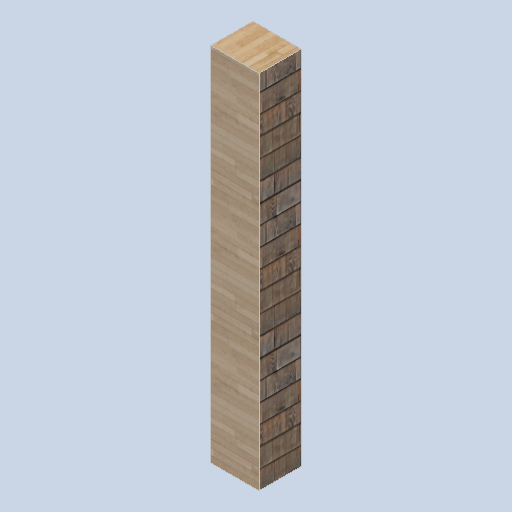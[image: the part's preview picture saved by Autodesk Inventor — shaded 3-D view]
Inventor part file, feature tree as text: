
AUTODESK INVENTOR PART (.ipt)
format: ipt  version: 2024.2 (Build 282272000, 272)  size: 173,568 bytes
history: native  units: in
note: dims shown in document units (in); Inventor stores cm internally (conversion verified against a paired STEP export)
features: other x3, sketch x1
ambient origin geometry x8: Origin, YZ Plane, XZ Plane, XY Plane, X Axis, Y Axis, Z Axis, Center Point
bodies: Solid1 (feature_tree)
feature tree (4):
  other  "support_column_02.ipt"
  other  "Solid1::support_column_02.ipt"
  other  "TaggingFeature1"
  sketch  "Sketch1"  dims[d0=0.3937in]
